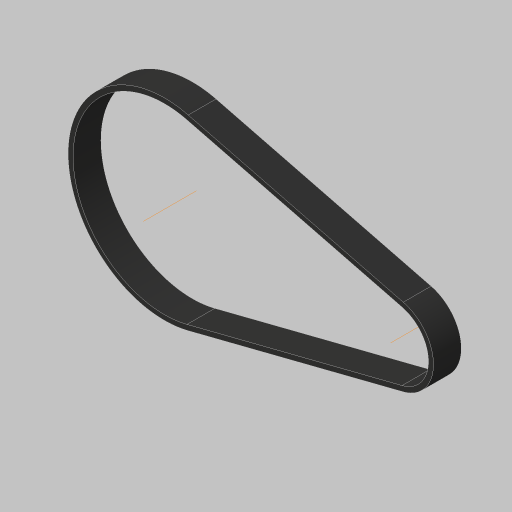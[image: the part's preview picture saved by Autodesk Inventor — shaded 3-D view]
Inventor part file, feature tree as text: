
AUTODESK INVENTOR PART (.ipt)
format: ipt  version: 2023.5 (Build 275446000, 446)  size: 171,008 bytes
history: native  units: in
note: dims shown in document units (in); Inventor stores cm internally (conversion verified against a paired STEP export)
features: sketch x3, extrude x1, other x1, projected_geometry x1
ambient origin geometry x8: Origin, YZ Plane, XZ Plane, XY Plane, X Axis, Y Axis, Z Axis, Center Point
bodies: Body1 (feature_tree)
feature tree (6):
  sketch  "Sketch2"  dims[d0=0.9023in d1=2.2558in]
  extrude  "Extrusion2"  Depth=2.2558in
  sketch  "Sketch5"  dims[d3=4.1041in d5=2.6664in d9=0.0787in d10=0.0598in d11=0.0299in d12=0.0219in d13=0.0219in d14=0.0059in d15=0.0059in d20=0.3346in d21=0.0in d22=0.0787in d23=0.0598in d24=0.0299in d25=0.0219in d26=0.0219in d27=0.0059in d28=0.0059in d29=0.0299in d30=0.0394in d31=0.0787in d32=0.0232in d34=0.0219in d35=0.0in d36=0.0in d37=0.0059in d38=0.0022in d39=0.0022in d40=0.0in d41=0.0in d42=0.0081in d43=0.0081in d44=0.0299in]
  other  "Work Axis1"
  sketch  "Sketch4"  dims[d2=1.1931in]
  projected_geometry  "Projected Loop1"
